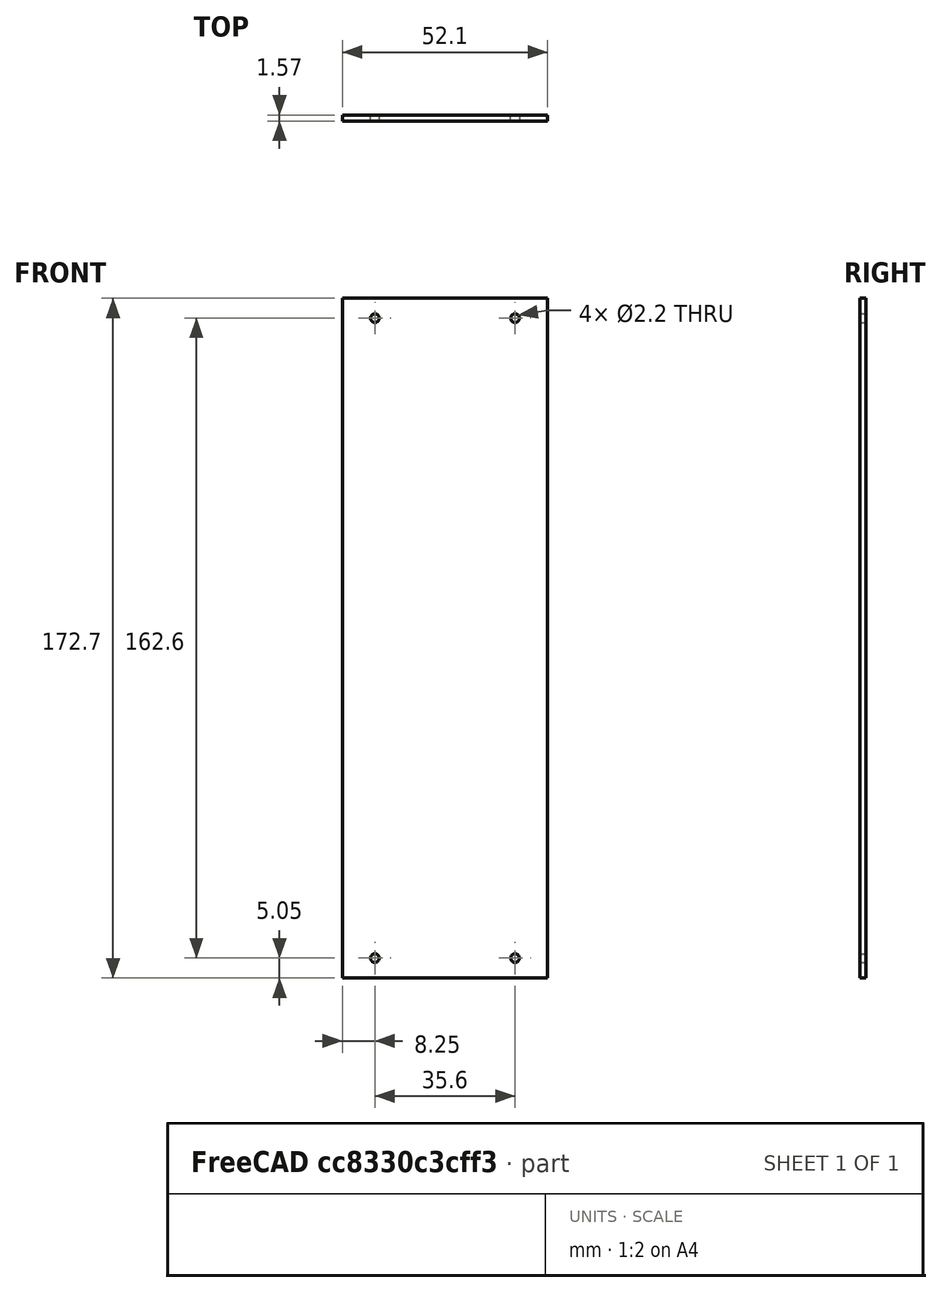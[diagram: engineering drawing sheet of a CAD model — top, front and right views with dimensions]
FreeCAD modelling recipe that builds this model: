
FCSTD DOCUMENT  (FreeCAD 1.0R39109 (Git))
Label: Protoboard
License: All rights reserved
LicenseURL: https://en.wikipedia.org/wiki/All_rights_reserved
objects: Spreadsheet::Sheet×1, Sketcher::SketchObject×1, PartDesign::Pad×1, PartDesign::Body×1
note: 6 computed .brp shape members not serialized (recipe doc carries the construction recipe); baked Part::Feature solids carry a one-line shape summary decoded from their .brp

FEATURE [Spreadsheet::Sheet] Spreadsheet004  label="ProtoboardSS"
  cells = A1='Total Length; B1(total_length)==172.7 mm; A2='Mount Hole Spacing Length; B2(mount_spacing_length)==162.6 mm; A3='Mount Hole Spacing Width; B3(mount_spacing_width)==35.6 mm; A4='Total Width; B4(total_width)==52.1 mm; A5='Pins Width; B5(pin_width)==157.4 mm; A6='One Side Pin Margin; B6(pin_margin)==(total_length - pin_width) / 2; A7='Pitch; B7(pitch)==2.54 mm; A8='Mount to Pin Offset; B8(mount_pin_offset)==(mount_spacing_length - pin_width) / 2; A9='PCB Thickness; B9(thickness)==1.57 mm; A10='Mount Hole Side Offset; B10(mount_hole_side_offset)==(total_width - mount_spacing_width) / 2; A11='Mount Hole Top Offset; B11(mount_top_offset)==(total_length - mount_spacing_length) / 2; A12='M2 Mount Hole Size; B12(mount_hole_diameter)==2.2 mm; A13='first_pin_row_start; B13(first_pin_row_start)==(total_length - pin_width) / 2
FEATURE [Sketcher::SketchObject] Sketch020
  ArcFitTolerance = 1e-06
  AttachmentSupport = -> [XZ_Plane009]
  FullyConstrained = true
  MakeInternals = false
  MapMode = 5
  Placement = pos=(0,0,0) rot=(1,0,0;1.5708rad)
  expr: Constraints[10] = <<ProtoboardSS>>.total_length
  expr: Constraints[14] = <<ProtoboardSS>>.mount_hole_diameter
  expr: Constraints[15] = <<ProtoboardSS>>.mount_top_offset
  expr: Constraints[16] = <<ProtoboardSS>>.mount_hole_side_offset
  expr: Constraints[17] = <<ProtoboardSS>>.mount_top_offset
  expr: Constraints[18] = <<ProtoboardSS>>.total_width - <<ProtoboardSS>>.mount_hole_side_offset
  expr: Constraints[19] = <<ProtoboardSS>>.mount_hole_side_offset
  expr: Constraints[20] = <<ProtoboardSS>>.mount_top_offset
  expr: Constraints[21] = <<ProtoboardSS>>.mount_hole_side_offset
  expr: Constraints[22] = <<ProtoboardSS>>.mount_top_offset
  expr: Constraints[9] = <<ProtoboardSS>>.total_width
  sketch-geometry (12):
    g0: LineSegment StartX=0 StartY=0 StartZ=0 EndX=52.1 EndY=0 EndZ=0
    g1: LineSegment StartX=52.1 StartY=0 StartZ=0 EndX=52.1 EndY=172.7 EndZ=0
    g2: LineSegment StartX=52.1 StartY=172.7 StartZ=0 EndX=0 EndY=172.7 EndZ=0
    g3: LineSegment StartX=0 StartY=172.7 StartZ=0 EndX=0 EndY=0 EndZ=0
    g4: Circle CenterX=8.25 CenterY=167.65 CenterZ=0 NormalX=0 NormalY=0 NormalZ=1 AngleXU=0 Radius=1.1
    g5: Circle CenterX=43.85 CenterY=167.65 CenterZ=0 NormalX=0 NormalY=0 NormalZ=1 AngleXU=0 Radius=1.1
    g6: Circle CenterX=43.85 CenterY=5.05 CenterZ=0 NormalX=0 NormalY=0 NormalZ=1 AngleXU=0 Radius=1.1
    g7: Circle CenterX=8.25 CenterY=5.05 CenterZ=0 NormalX=0 NormalY=0 NormalZ=1 AngleXU=0 Radius=1.1
    g8: GeomPoint X=8.25 Y=5.05 Z=0
    g9: GeomPoint X=43.85 Y=5.05 Z=0
    g10: GeomPoint X=43.85 Y=167.65 Z=0
    g11: GeomPoint X=8.25 Y=167.65 Z=0
  constraints (27):
    c: Coincident(g0,g1)
    c: Coincident(g1,g2)
    c: Coincident(g2,g3)
    c: Coincident(g3,g0)
    c: Horizontal(g0)
    c: Horizontal(g2)
    c: Vertical(g1)
    c: Vertical(g3)
    c: Coincident(g-1,g0)
    c: Distance(g0) = 52.1
    c: Distance(g3) = 172.7
    c: Equal(g7,g6)
    c: Equal(g7,g5)
    c: Equal(g7,g4)
    c: Diameter(g7) = 2.2
    c: Distance(g4,g2) = 5.05
    c: Distance(g4,g3) = 8.25
    c: Distance(g5,g2) = 5.05
    c: Distance(g5,g3) = 43.85
    c: Distance(g7,g3) = 8.25
    c: DistanceY(g-1,g7) = 5.05
    c: Distance(g6,g1) = 8.25
    c: Distance(g6,g0) = 5.05
    c: Coincident(g8,g7)
    c: Coincident(g9,g6)
    c: Coincident(g10,g5)
    c: Coincident(g11,g4)
FEATURE [PartDesign::Pad] Pad007  label="Protoboard Pad"
  Direction = (0,-1,2e-16)
  Length = 1.57
  Length2 = 10
  Placement = pos=(0,0,0) rot=(1,0,0;1.5708rad)
  Profile = -> Sketch020
  ReferenceAxis = -> Sketch020 [N_Axis]
  Refine = true
  Suppressed = false
  Type = 0
  expr: Length = <<ProtoboardSS>>.thickness
FEATURE [PartDesign::Body] Body007  label="Protoboard Body"
  AllowCompound = false
  Group = -> [Sketch020,Pad007]
  Origin = -> Origin009
  Tip = -> Pad007
